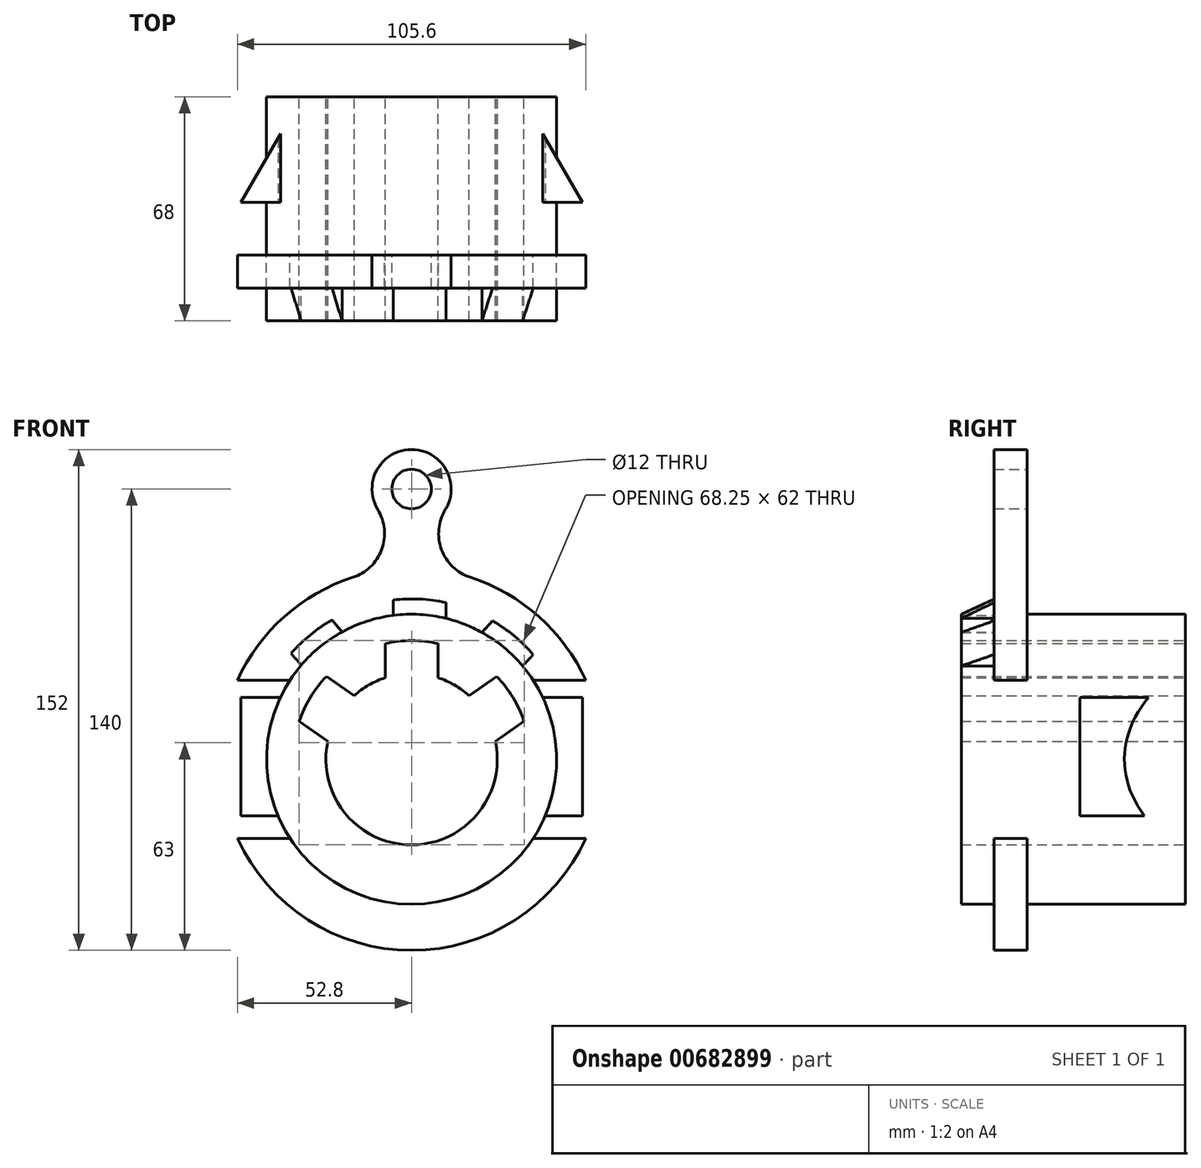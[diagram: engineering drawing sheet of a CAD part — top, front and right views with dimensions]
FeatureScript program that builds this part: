
annotation { "Feature Type Name" : "Feature", "Feature Type Description" : "" }
export const myFeature = defineFeature(function(context is Context, id is Id, definition is map)
    precondition{}
    {
        {
            var Q0;
            Q0=qCreatedBy(makeId("Front.planeOp"),FACE);
            var sketch = newSketch(context, id + "F0", { "sketchPlane" : qUnion([Q0])});
            skCircle(sketch, "E0", {"center": v(0, 0) * mm, "radius": 44 * mm});
            skArc(sketch, "E1", {"start": v(-8, 24.74) * mm, "mid": v(-13, 22.52) * mm, "end": v(-17.42, 19.3) * mm});
            skArc(sketch, "E2", {"start": v(-25.76, 25.15) * mm, "mid": v(-30.71, 18.78) * mm, "end": v(-34.12, 11.47) * mm});
            skLineSegment(sketch, "E3", {"start": v(-8, 24.74) * mm, "end": v(-8, 35.1) * mm});
            skLineSegment(sketch, "E4", {"start": v(8, 24.74) * mm, "end": v(8, 35.1) * mm});
            skPoint(sketch, "E5.start.orphan", {"position": v(0, 64.98) * mm});
            skLineSegment(sketch, "E6", {"start": v(-17.42, 19.3) * mm, "end": v(-25.76, 25.15) * mm});
            skLineSegment(sketch, "E7", {"start": v(-25.44, 5.39) * mm, "end": v(-34.12, 11.47) * mm});
            skArc(sketch, "E8.trimOffspring", {"start": v(-25.44, 5.39) * mm, "mid": v(0, -26) * mm, "end": v(25.44, 5.39) * mm});
            skLineSegment(sketch, "E9", {"start": v(17.42, 19.3) * mm, "end": v(25.76, 25.15) * mm});
            skLineSegment(sketch, "E10", {"start": v(25.44, 5.39) * mm, "end": v(34.12, 11.47) * mm});
            skArc(sketch, "E11.trimOffspring", {"start": v(17.42, 19.3) * mm, "mid": v(13, 22.52) * mm, "end": v(8, 24.74) * mm});
            skArc(sketch, "E12.trimOffspring", {"start": v(8, 35.1) * mm, "mid": v(0, 36) * mm, "end": v(-8, 35.1) * mm});
            skArc(sketch, "E13.trimOffspring", {"start": v(34.12, 11.47) * mm, "mid": v(30.71, 18.78) * mm, "end": v(25.76, 25.15) * mm});
            skSolve(sketch);
        }
        {
            var Q0;
            Q0=makeQuery(id+"F0.imprint","IMPRINT",FACE,{"disambiguationData":[TD([[makeQuery(id+"F0.imprint","IMPRINT",EDGE,{"derivedFrom":sQuery(id+"F0.wireOp",EDGE,"E0")}),1.0]])]});
            extrude(context, id + "F1", {"entities" : qUnion([Q0]), "depth" : 68 * mm, "offsetDistance" : 25 * mm});
        }
        {
            var Q0;
            Q0=qCreatedBy(makeId("Front.planeOp"),FACE);
            cPlane(context, id + "F2", {"entities" : qUnion([Q0]), "cplaneType" : CPlaneType.OFFSET, "offset" : 48 * mm, "width" : 150 * mm, "height" : 150 * mm});
        }
        {
            var Q0;
            Q0=qCreatedBy(id+"F2.planeOp",FACE);
            var sketch = newSketch(context, id + "F3", { "sketchPlane" : qUnion([Q0])});
            skArc(sketch, "E14", {"start": v(-17.9, 55.17) * mm, "mid": v(-38.63, 43.26) * mm, "end": v(-52.8, 24) * mm});
            skCircle(sketch, "E15", {"center": v(0, 82) * mm, "radius": 6 * mm});
            skArc(sketch, "E16", {"start": v(10.25, 75.76) * mm, "mid": v(0, 94) * mm, "end": v(-10.25, 75.76) * mm});
            skArc(sketch, "E17", {"start": v(-17.9, 55.17) * mm, "mid": v(-9.09, 63.62) * mm, "end": v(-10.25, 75.76) * mm});
            skArc(sketch, "E18", {"start": v(10.25, 75.76) * mm, "mid": v(9.09, 63.62) * mm, "end": v(17.9, 55.17) * mm});
            skPoint(sketch, "E19.start.orphan", {"position": v(0, -73.3) * mm});
            skArc(sketch, "E20.trimOffspring", {"start": v(-52.8, -24) * mm, "mid": v(0, -58) * mm, "end": v(52.8, -24) * mm});
            skArc(sketch, "E21.trimOffspring", {"start": v(52.8, 24) * mm, "mid": v(38.63, 43.26) * mm, "end": v(17.9, 55.17) * mm});
            skCircle(sketch, "E22", {"center": v(0, 0) * mm, "radius": 44 * mm});
            skLineSegment(sketch, "E23", {"start": v(-52.8, 24) * mm, "end": v(-36.88, 24) * mm});
            skLineSegment(sketch, "E24", {"start": v(52.8, 24) * mm, "end": v(36.88, 24) * mm});
            skLineSegment(sketch, "E25", {"start": v(-52.8, -24) * mm, "end": v(-36.88, -24) * mm});
            skLineSegment(sketch, "E26", {"start": v(52.8, -24) * mm, "end": v(36.88, -24) * mm});
            skSolve(sketch);
        }
        {
            var Q0;
            Q0=makeQuery(id+"F3.imprint","IMPRINT",FACE,{"disambiguationData":[TD([[makeQuery(id+"F3.imprint","IMPRINT",EDGE,{"derivedFrom":sQuery(id+"F3.wireOp",EDGE,"E14")}),1.0]])]});
            var Q1;
            Q1=makeQuery(id+"F3.imprint","IMPRINT",FACE,{"disambiguationData":[TD([[makeQuery(id+"F3.imprint","IMPRINT",EDGE,{"derivedFrom":sQuery(id+"F3.wireOp",EDGE,"E20.trimOffspring")}),1.0]])]});
            extrude(context, id + "F4", {"entities" : qUnion([Q0, Q1]), "operationType" : NewBodyOperationType.ADD, "depth" : 10 * mm, "offsetDistance" : 25 * mm});
        }
        {
            var Q0;
            Q0=qCreatedBy(id+"F2.planeOp",FACE);
            cPlane(context, id + "F5", {"entities" : qUnion([Q0]), "cplaneType" : CPlaneType.OFFSET, "offset" : 10 * mm, "width" : 150 * mm, "height" : 150 * mm});
        }
        {
            var Q0;
            Q0=qCreatedBy(id+"F5.planeOp",FACE);
            var sketch = newSketch(context, id + "F6", { "sketchPlane" : qUnion([Q0])});
            skArc(sketch, "E27", {"start": v(37.12, 31.99) * mm, "mid": v(31.39, 37.63) * mm, "end": v(24.81, 42.25) * mm});
            skCircle(sketch, "E28", {"center": v(0, 0) * mm, "radius": 44 * mm});
            skLineSegment(sketch, "E29", {"start": v(-36.76, 32.4) * mm, "end": v(-33.5, 28.52) * mm});
            skLineSegment(sketch, "E30", {"start": v(-24.36, 42.52) * mm, "end": v(-21.09, 38.62) * mm});
            skLineSegment(sketch, "E31", {"start": v(-5.59, 48.68) * mm, "end": v(-5.59, 43.64) * mm});
            skLineSegment(sketch, "E32", {"start": v(10.41, 47.88) * mm, "end": v(10.41, 42.75) * mm});
            skLineSegment(sketch, "E33", {"start": v(24.81, 42.25) * mm, "end": v(21.3, 38.5) * mm});
            skLineSegment(sketch, "E34", {"start": v(37.12, 31.99) * mm, "end": v(33.68, 28.3) * mm});
            skArc(sketch, "E35.trimOffspring", {"start": v(-24.36, 42.52) * mm, "mid": v(-30.97, 37.97) * mm, "end": v(-36.76, 32.4) * mm});
            skArc(sketch, "E36.trimOffspring", {"start": v(10.41, 47.88) * mm, "mid": v(2.45, 48.94) * mm, "end": v(-5.59, 48.68) * mm});
            skSolve(sketch);
        }
        {
            var Q0;
            {var subQ0=sQuery(id+"F6.wireOp",EDGE,"E29");Q0=makeQuery(id+"F6.imprint","IMPRINT",FACE,{"disambiguationData":[TD([[makeQuery(id+"F6.imprint","IMPRINT",EDGE,{"derivedFrom":subQ0}),1.0]])]});}
            var Q1;
            {var subQ0=sQuery(id+"F6.wireOp",EDGE,"E31");Q1=makeQuery(id+"F6.imprint","IMPRINT",FACE,{"disambiguationData":[TD([[makeQuery(id+"F6.imprint","IMPRINT",EDGE,{"derivedFrom":subQ0}),1.0]])]});}
            var Q2;
            Q2=makeQuery(id+"F6.imprint","IMPRINT",FACE,{"disambiguationData":[TD([[makeQuery(id+"F6.imprint","IMPRINT",EDGE,{"derivedFrom":sQuery(id+"F6.wireOp",EDGE,"E27")}),1.0]])]});
            extrude(context, id + "F7", {"entities" : qUnion([Q0, Q1, Q2]), "operationType" : NewBodyOperationType.ADD, "depth" : 10 * mm, "offsetDistance" : 25 * mm});
        }
        {
            var Q0;
            Q0=makeQuery(id+"F7.opExtrude","CAP_EDGE",EDGE,{"disambiguationData":[OSD([sQuery(id+"F6.wireOp",EDGE,"E27")])],"isStart":false});
            var Q1;
            Q1=makeQuery(id+"F7.opExtrude","CAP_EDGE",EDGE,{"disambiguationData":[OSD([sQuery(id+"F6.wireOp",EDGE,"E36.trimOffspring")])],"isStart":false});
            var Q2;
            Q2=makeQuery(id+"F7.opExtrude","CAP_EDGE",EDGE,{"disambiguationData":[OSD([sQuery(id+"F6.wireOp",EDGE,"E35.trimOffspring")])],"isStart":false});
            chamfer(context, id + "F8", {"entities" : qUnion([Q0, Q1, Q2]), "chamferType" : ChamferType.OFFSET_ANGLE, "width" : 5 * mm, "oppositeDirection" : false, "angle" : 65 * degree, "tangentPropagation" : true});
        }
        {
            var Q0;
            Q0=qCreatedBy(makeId("Front.planeOp"),FACE);
            cPlane(context, id + "F9", {"entities" : qUnion([Q0]), "cplaneType" : CPlaneType.OFFSET, "offset" : 32 * mm, "width" : 150 * mm, "height" : 150 * mm});
        }
        {
            var Q0;
            Q0=qCreatedBy(id+"F9.planeOp",FACE);
            var sketch = newSketch(context, id + "F10", { "sketchPlane" : qUnion([Q0])});
            skCircle(sketch, "E37", {"center": v(0, 0) * mm, "radius": 44 * mm});
            skLineSegment(sketch, "E38", {"start": v(39.78, 18.8) * mm, "end": v(51.78, 18.8) * mm});
            skLineSegment(sketch, "E39", {"start": v(51.78, 18.8) * mm, "end": v(51.78, -17.2) * mm});
            skLineSegment(sketch, "E40", {"start": v(51.78, -17.2) * mm, "end": v(40.5, -17.2) * mm});
            skLineSegment(sketch, "E41", {"start": v(-39.78, 18.8) * mm, "end": v(-51.78, 18.8) * mm});
            skLineSegment(sketch, "E42", {"start": v(-51.78, 18.8) * mm, "end": v(-51.78, -17.2) * mm});
            skLineSegment(sketch, "E43", {"start": v(-51.78, -17.2) * mm, "end": v(-40.5, -17.2) * mm});
            skSolve(sketch);
        }
        {
            var Q0;
            {var subQ0=sQuery(id+"F10.wireOp",EDGE,"E38");Q0=makeQuery(id+"F10.imprint","IMPRINT",FACE,{"disambiguationData":[TD([[makeQuery(id+"F10.imprint","IMPRINT",EDGE,{"derivedFrom":subQ0}),-1.0]])]});}
            var Q1;
            {var subQ0=sQuery(id+"F10.wireOp",EDGE,"E41");Q1=makeQuery(id+"F10.imprint","IMPRINT",FACE,{"disambiguationData":[TD([[makeQuery(id+"F10.imprint","IMPRINT",EDGE,{"derivedFrom":subQ0}),1.0]])]});}
            extrude(context, id + "F11", {"entities" : qUnion([Q0, Q1]), "operationType" : NewBodyOperationType.ADD, "oppositeDirection" : true, "depth" : 25 * mm, "offsetDistance" : 25 * mm});
        }
        {
            var Q0;
            Q0=makeQuery(id+"F11.opExtrude","CAP_EDGE",EDGE,{"disambiguationData":[OSD([sQuery(id+"F10.wireOp",EDGE,"E39")])],"isStart":false});
            chamfer(context, id + "F12", {"entities" : qUnion([Q0]), "chamferType" : ChamferType.OFFSET_ANGLE, "width" : 25 * mm, "oppositeDirection" : true, "angle" : 30 * degree, "tangentPropagation" : true});
        }
        {
            var Q0;
            Q0=makeQuery(id+"F11.opExtrude","CAP_EDGE",EDGE,{"disambiguationData":[OSD([sQuery(id+"F10.wireOp",EDGE,"E42")])],"isStart":false});
            chamfer(context, id + "F13", {"entities" : qUnion([Q0]), "chamferType" : ChamferType.OFFSET_ANGLE, "width" : 25 * mm, "oppositeDirection" : false, "angle" : 30 * degree, "tangentPropagation" : true});
        }
    });
